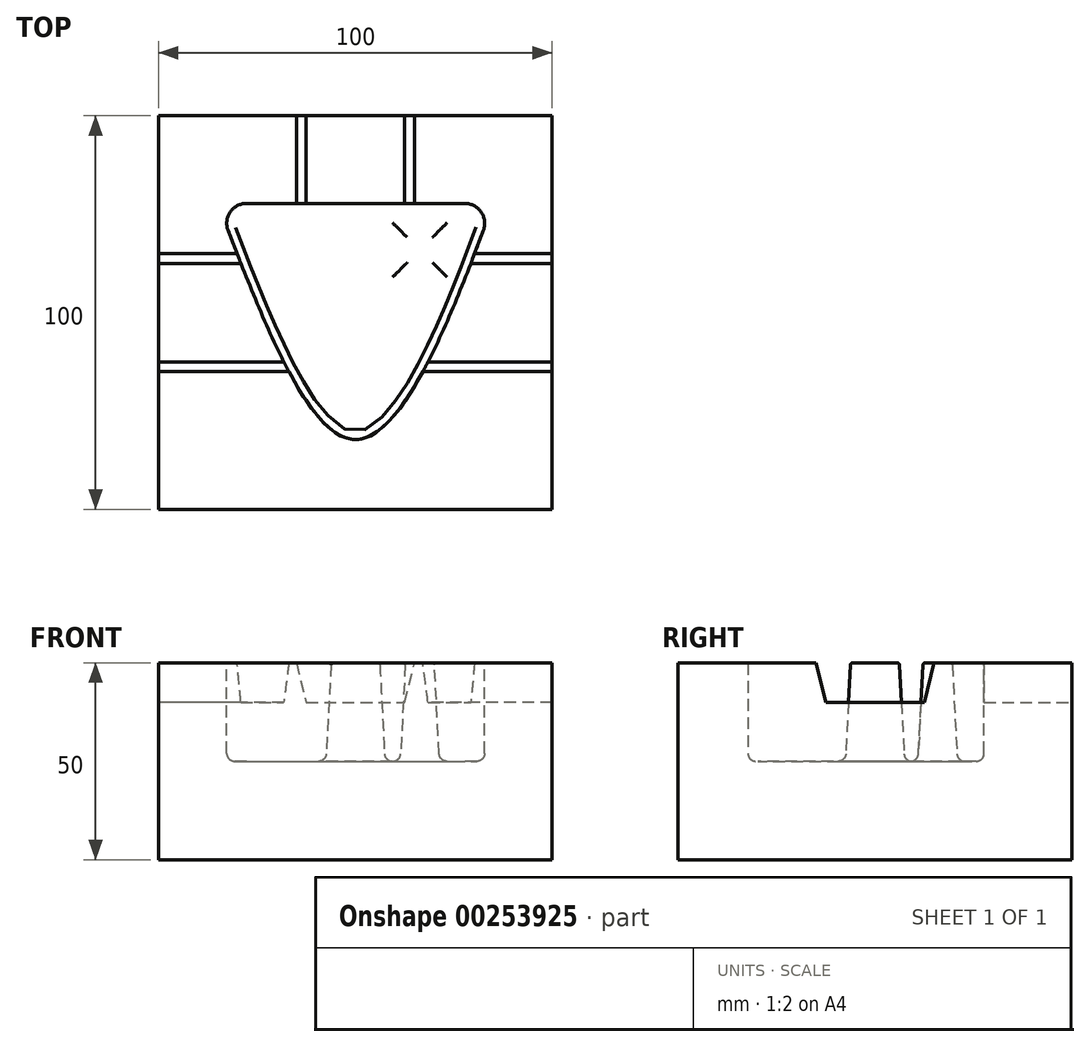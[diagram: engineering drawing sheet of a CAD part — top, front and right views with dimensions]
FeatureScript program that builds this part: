
annotation { "Feature Type Name" : "Feature", "Feature Type Description" : "" }
export const myFeature = defineFeature(function(context is Context, id is Id, definition is map)
    precondition{}
    {
        {
            var Q0;
            Q0=qCreatedBy(makeId("Top.planeOp"),FACE);
            var sketch = newSketch(context, id + "F0", { "sketchPlane" : qUnion([Q0])});
            skLineSegment(sketch, "E0.bottom", {"start": v(50, -50) * mm, "end": v(-50, -50) * mm});
            skLineSegment(sketch, "E0.top", {"start": v(50, 50) * mm, "end": v(-50, 50) * mm});
            skLineSegment(sketch, "E0.left", {"start": v(50, -50) * mm, "end": v(50, 50) * mm});
            skLineSegment(sketch, "E0.right", {"start": v(-50, -50) * mm, "end": v(-50, 50) * mm});
            skPoint(sketch, "E0.middle", {"position": v(0, 0) * mm});
            skSolve(sketch);
        }
        {
            var Q0;
            Q0=makeQuery(id+"F0.imprint","IMPRINT",FACE,{"disambiguationData":[TD([[makeQuery(id+"F0.imprint","IMPRINT",EDGE,{"derivedFrom":sQuery(id+"F0.wireOp",EDGE,"E0.bottom")}),-1.0]])]});
            extrude(context, id + "F1", {"entities" : qUnion([Q0]), "depth" : 50 * mm});
        }
        {
            var Q0;
            Q0=makeQuery(id+"F1.opExtrude","CAP_FACE",FACE,{"disambiguationData":[OSD([sQuery(id+"F0.wireOp",EDGE,"E0.bottom"),sQuery(id+"F0.wireOp",EDGE,"E0.top"),sQuery(id+"F0.wireOp",EDGE,"E0.left"),sQuery(id+"F0.wireOp",EDGE,"E0.right")])],"isStart":false});
            var sketch = newSketch(context, id + "F2", { "sketchPlane" : qUnion([Q0])});
            skFitSpline(sketch, "E1", {"points": [v(-35, 27.73) * mm, v(0, -32.27) * mm, v(35, 27.73) * mm], "startDerivative": vector(58.01, -148.12) * mm, "endDerivative": vector(54.3, 148.62) * mm});
            skLineSegment(sketch, "E2", {"start": v(-27.7, 27.73) * mm, "end": v(27.84, 27.73) * mm});
            skArc(sketch, "E3.filletArc", {"start": v(-27.7, 27.73) * mm, "mid": v(-31.82, 25.55) * mm, "end": v(-32.35, 20.92) * mm});
            skArc(sketch, "E4.filletArc", {"start": v(32.52, 20.99) * mm, "mid": v(31.94, 25.58) * mm, "end": v(27.84, 27.73) * mm});
            skSolve(sketch);
        }
        {
            var Q0;
            Q0=makeQuery(id+"F2.imprint","IMPRINT",FACE,{"disambiguationData":[TD([[makeQuery(id+"F2.imprint","IMPRINT",EDGE,{"derivedFrom":sQuery(id+"F2.wireOp",EDGE,"E1")}),1.0]])]});
            extrude(context, id + "F3", {"entities" : qUnion([Q0]), "operationType" : NewBodyOperationType.REMOVE, "oppositeDirection" : true, "depth" : 25 * mm});
        }
        {
            var Q0;
            Q0=makeQuery(id+"F1.opExtrude","SWEPT_FACE",FACE,{"disambiguationData":[OSD([sQuery(id+"F0.wireOp",EDGE,"E0.top")])]});
            var sketch = newSketch(context, id + "F4", { "sketchPlane" : qUnion([Q0])});
            skLineSegment(sketch, "E5", {"start": v(-15, 50) * mm, "end": v(15, 50) * mm});
            skLineSegment(sketch, "E6", {"start": v(15, 50) * mm, "end": v(12.5, 40) * mm});
            skLineSegment(sketch, "E7", {"start": v(12.5, 40) * mm, "end": v(-12.5, 40) * mm});
            skLineSegment(sketch, "E8", {"start": v(-12.5, 40) * mm, "end": v(-15, 50) * mm});
            skSolve(sketch);
        }
        {
            var Q0;
            Q0=makeQuery(id+"F4.imprint","IMPRINT",FACE,{"disambiguationData":[TD([[makeQuery(id+"F4.imprint","IMPRINT",EDGE,{"derivedFrom":sQuery(id+"F4.wireOp",EDGE,"E5")}),-1.0]])]});
            extrude(context, id + "F5", {"entities" : qUnion([Q0]), "operationType" : NewBodyOperationType.REMOVE, "endBound" : BoundingType.UP_TO_NEXT, "oppositeDirection" : true, "depth" : 25 * mm});
        }
        {
            var Q0;
            Q0=makeQuery(id+"F1.opExtrude","SWEPT_FACE",FACE,{"disambiguationData":[OSD([sQuery(id+"F0.wireOp",EDGE,"E0.right")])]});
            var sketch = newSketch(context, id + "F6", { "sketchPlane" : qUnion([Q0])});
            skLineSegment(sketch, "E9", {"start": v(-15, 50) * mm, "end": v(15, 50) * mm});
            skLineSegment(sketch, "E10", {"start": v(15, 50) * mm, "end": v(12.5, 40) * mm});
            skLineSegment(sketch, "E11", {"start": v(12.5, 40) * mm, "end": v(-12.5, 40) * mm});
            skLineSegment(sketch, "E12", {"start": v(-12.5, 40) * mm, "end": v(-15, 50) * mm});
            skSolve(sketch);
        }
        {
            var Q0;
            Q0=qSketchRegion(id+"F6",true);
            extrude(context, id + "F7", {"entities" : qUnion([Q0]), "operationType" : NewBodyOperationType.REMOVE, "oppositeDirection" : true, "depth" : 100 * mm});
        }
        {
            var Q0;
            Q0=makeQuery(id+"F3.boolean.opBoolean","COPY",FACE,{"derivedFrom":makeQuery(id+"F3.opExtrude","CAP_FACE",FACE,{"disambiguationData":[OSD([sQuery(id+"F2.wireOp",EDGE,"E1"),sQuery(id+"F2.wireOp",EDGE,"E2"),sQuery(id+"F2.wireOp",EDGE,"E3.filletArc"),sQuery(id+"F2.wireOp",EDGE,"E4.filletArc")])],"isStart":false})});
            var sketch = newSketch(context, id + "F8", { "sketchPlane" : qUnion([Q0])});
            skCircle(sketch, "E13", {"center": v(0, 0) * mm, "radius": 7.5 * mm});
            skLineSegment(sketch, "E14.bottom", {"start": v(21.38, 10.92) * mm, "end": v(11.38, 10.92) * mm});
            skLineSegment(sketch, "E14.top", {"start": v(21.38, 20.92) * mm, "end": v(11.38, 20.92) * mm});
            skLineSegment(sketch, "E14.left", {"start": v(21.38, 10.92) * mm, "end": v(21.38, 20.92) * mm});
            skLineSegment(sketch, "E14.right", {"start": v(11.38, 10.92) * mm, "end": v(11.38, 20.92) * mm});
            skPoint(sketch, "E14.middle", {"position": v(16.38, 15.92) * mm});
            skSolve(sketch);
        }
        {
            var Q0;
            Q0=makeQuery(id+"F8.imprint","IMPRINT",FACE,{"disambiguationData":[TD([[makeQuery(id+"F8.imprint","IMPRINT",EDGE,{"derivedFrom":sQuery(id+"F8.wireOp",EDGE,"E13")}),1.0]])]});
            var Q1;
            Q1=makeQuery(id+"F8.imprint","IMPRINT",FACE,{"disambiguationData":[TD([[makeQuery(id+"F8.imprint","IMPRINT",EDGE,{"derivedFrom":sQuery(id+"F8.wireOp",EDGE,"E14.bottom")}),-1.0]])]});
            extrude(context, id + "F9", {"entities" : qUnion([Q0, Q1]), "operationType" : NewBodyOperationType.ADD, "depth" : 25 * mm, "hasDraft" : true, "draftAngle" : 3 * degree, "draftPullDirection" : true});
        }
        {
            var Q0;
            Q0=makeQuery(id+"F3.boolean.opBoolean","COPY",FACE,{"derivedFrom":makeQuery(id+"F3.opExtrude","CAP_FACE",FACE,{"disambiguationData":[OSD([sQuery(id+"F2.wireOp",EDGE,"E1"),sQuery(id+"F2.wireOp",EDGE,"E2"),sQuery(id+"F2.wireOp",EDGE,"E3.filletArc"),sQuery(id+"F2.wireOp",EDGE,"E4.filletArc")])],"isStart":false})});
            fillet(context, id + "F10", {"entities" : qUnion([Q0]), "radius" : 2 * mm, "tangentPropagation" : true, "allowEdgeOverflow" : false});
        }
        {
            var Q0;
            Q0=makeQuery(id+"F9.opExtrude","CAP_EDGE",EDGE,{"disambiguationData":[OSD([sQuery(id+"F8.wireOp",EDGE,"E13")])],"isStart":false});
            fillet(context, id + "F11", {"entities" : qUnion([Q0]), "radius" : 0.5 * mm, "tangentPropagation" : true, "allowEdgeOverflow" : false});
        }
        {
            var Q0;
            Q0=makeQuery(id+"F9.opExtrude","CAP_EDGE",EDGE,{"disambiguationData":[OSD([sQuery(id+"F8.wireOp",EDGE,"E14.bottom")])],"isStart":false});
            var Q1;
            Q1=makeQuery(id+"F9.opExtrude","CAP_EDGE",EDGE,{"disambiguationData":[OSD([sQuery(id+"F8.wireOp",EDGE,"E14.right")])],"isStart":false});
            var Q2;
            Q2=makeQuery(id+"F9.opExtrude","CAP_EDGE",EDGE,{"disambiguationData":[OSD([sQuery(id+"F8.wireOp",EDGE,"E14.top")])],"isStart":false});
            var Q3;
            Q3=makeQuery(id+"F9.opExtrude","CAP_EDGE",EDGE,{"disambiguationData":[OSD([sQuery(id+"F8.wireOp",EDGE,"E14.left")])],"isStart":false});
            fillet(context, id + "F12", {"entities" : qUnion([Q0, Q1, Q2, Q3]), "radius" : 0.5 * mm, "tangentPropagation" : true, "allowEdgeOverflow" : false});
        }
    });
